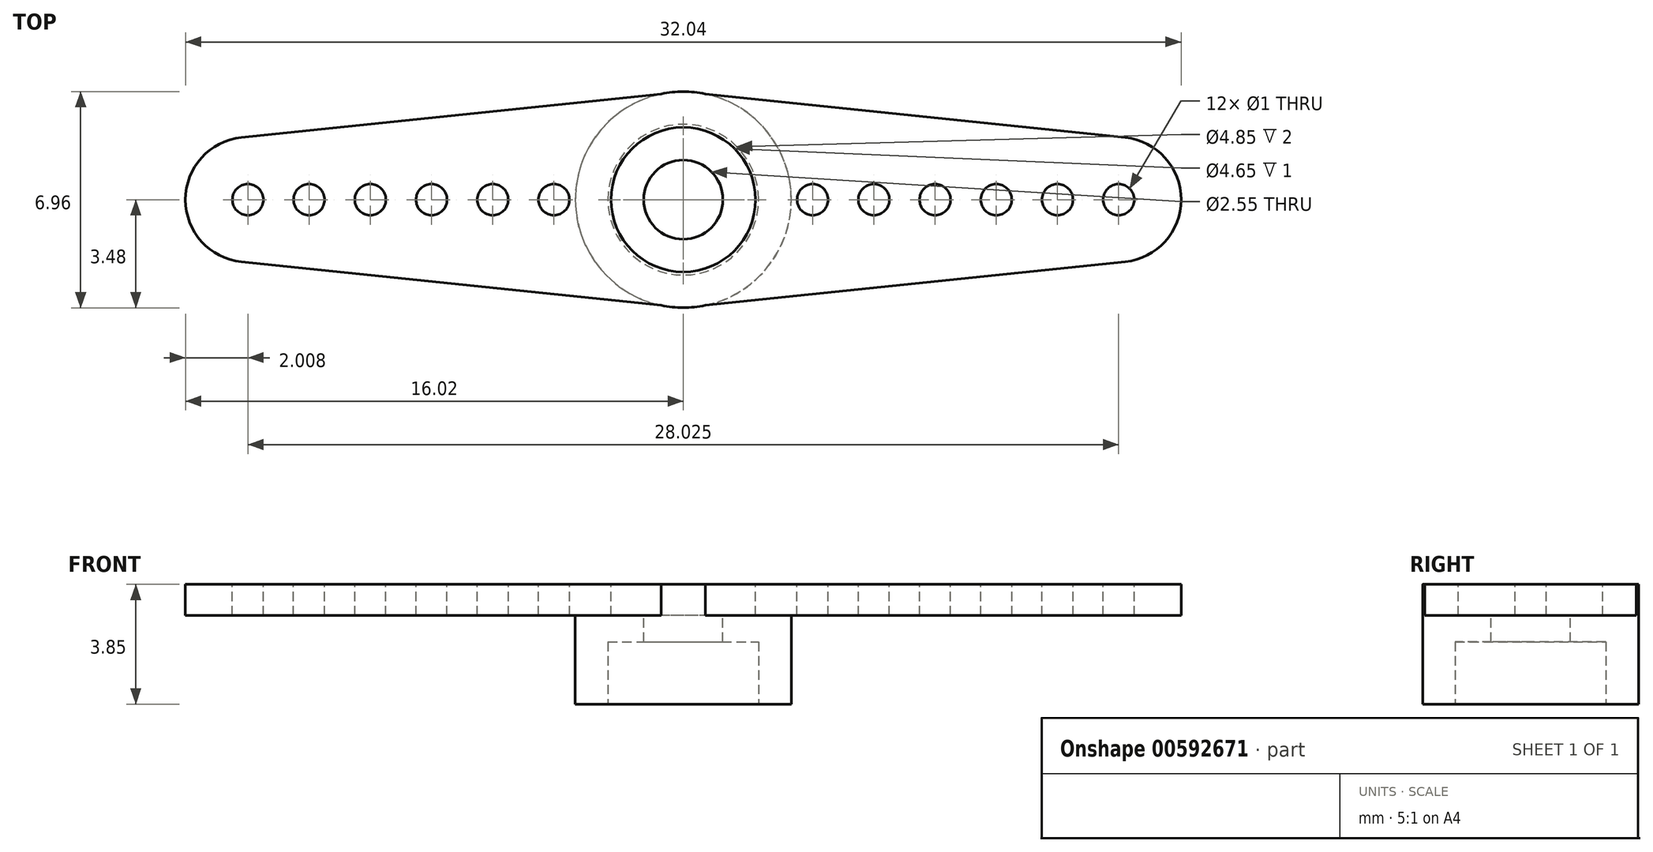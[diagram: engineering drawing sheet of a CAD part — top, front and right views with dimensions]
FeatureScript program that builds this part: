
annotation { "Feature Type Name" : "Feature", "Feature Type Description" : "" }
export const myFeature = defineFeature(function(context is Context, id is Id, definition is map)
    precondition{}
    {
        {
            var Q0;
            Q0=qCreatedBy(makeId("Top.planeOp"),FACE);
            var sketch = newSketch(context, id + "F0", { "sketchPlane" : qUnion([Q0])});
            skCircle(sketch, "E0", {"center": v(0, 0) * mm, "radius": 3.48 * mm});
            skSolve(sketch);
        }
        {
            var Q0;
            Q0=makeQuery(id+"F0.imprint","IMPRINT",FACE,{"disambiguationData":[TD([[makeQuery(id+"F0.imprint","IMPRINT",EDGE,{"derivedFrom":sQuery(id+"F0.wireOp",EDGE,"E0")}),1.0]])]});
            extrude(context, id + "F1", {"entities" : qUnion([Q0]), "depth" : 3.85 * mm, "offsetDistance" : 25 * mm});
        }
        {
            var Q0;
            Q0=makeQuery(id+"F1.opExtrude","CAP_FACE",FACE,{"disambiguationData":[OSD([sQuery(id+"F0.wireOp",EDGE,"E0")])],"isStart":true});
            var sketch = newSketch(context, id + "F2", { "sketchPlane" : qUnion([Q0])});
            skCircle(sketch, "E1", {"center": v(0, 0) * mm, "radius": 2.43 * mm});
            skSolve(sketch);
        }
        {
            var Q0;
            Q0=qSketchRegion(id+"F2",true);
            extrude(context, id + "F3", {"entities" : qUnion([Q0]), "operationType" : NewBodyOperationType.REMOVE, "oppositeDirection" : true, "depth" : 2 * mm, "offsetDistance" : 25 * mm});
        }
        {
            var Q0;
            Q0=makeQuery(id+"F1.opExtrude","CAP_FACE",FACE,{"disambiguationData":[OSD([sQuery(id+"F0.wireOp",EDGE,"E0")])],"isStart":false});
            var sketch = newSketch(context, id + "F4", { "sketchPlane" : qUnion([Q0])});
            skArc(sketch, "E2.0", {"start": v(0, 3.48) * mm, "mid": v(-3.48, 0) * mm, "end": v(0, -3.48) * mm});
            skLineSegment(sketch, "E3", {"start": v(0, 3.47) * mm, "end": v(14.22, 2) * mm});
            skLineSegment(sketch, "E4", {"start": v(0, -3.48) * mm, "end": v(14.22, -2) * mm});
            skLineSegment(sketch, "E5", {"start": v(0, 0) * mm, "end": v(14.22, 0) * mm, "construction": true});
            skLineSegment(sketch, "E6", {"start": v(14.22, 2) * mm, "end": v(14.22, 0) * mm, "construction": true});
            skLineSegment(sketch, "E7", {"start": v(14.22, 0) * mm, "end": v(14.22, -2) * mm, "construction": true});
            skArc(sketch, "E8", {"start": v(14.22, 2) * mm, "mid": v(16.02, 0) * mm, "end": v(14.22, -2) * mm});
            skSolve(sketch);
        }
        {
            var Q0;
            Q0=qSketchRegion(id+"F4",true);
            extrude(context, id + "F5", {"entities" : qUnion([Q0]), "operationType" : NewBodyOperationType.ADD, "oppositeDirection" : true, "depth" : 1 * mm, "offsetDistance" : 25 * mm});
        }
        {
            var Q0;
            Q0=makeQuery(id+"F5.boolean.opBoolean","MERGE",FACE,{"derivedFrom":[makeQuery(id+"F1.opExtrude","CAP_FACE",FACE,{"disambiguationData":[OSD([sQuery(id+"F0.wireOp",EDGE,"E0")])],"isStart":false}),makeQuery(id+"F5.opExtrude","CAP_FACE",FACE,{"disambiguationData":[OSD([sQuery(id+"F4.wireOp",EDGE,"E2.0"),sQuery(id+"F4.wireOp",EDGE,"E3"),sQuery(id+"F4.wireOp",EDGE,"E4"),sQuery(id+"F4.wireOp",EDGE,"E8")])],"isStart":true})]});
            var sketch = newSketch(context, id + "F6", { "sketchPlane" : qUnion([Q0])});
            skCircle(sketch, "E9", {"center": v(0, 0) * mm, "radius": 2.33 * mm});
            skSolve(sketch);
        }
        {
            var Q0;
            Q0=qSketchRegion(id+"F6",true);
            extrude(context, id + "F7", {"entities" : qUnion([Q0]), "operationType" : NewBodyOperationType.REMOVE, "oppositeDirection" : true, "depth" : 1 * mm, "offsetDistance" : 25 * mm});
        }
        {
            var Q0;
            Q0=makeQuery(id+"F7.boolean.opBoolean","COPY",FACE,{"derivedFrom":makeQuery(id+"F7.opExtrude","CAP_FACE",FACE,{"disambiguationData":[OSD([sQuery(id+"F6.wireOp",EDGE,"E9")])],"isStart":false})});
            var sketch = newSketch(context, id + "F8", { "sketchPlane" : qUnion([Q0])});
            skCircle(sketch, "E10", {"center": v(0, 0) * mm, "radius": 1.27 * mm});
            skSolve(sketch);
        }
        {
            var Q0;
            Q0=qSketchRegion(id+"F8",true);
            extrude(context, id + "F9", {"entities" : qUnion([Q0]), "operationType" : NewBodyOperationType.REMOVE, "endBound" : BoundingType.THROUGH_ALL, "oppositeDirection" : true, "depth" : 25 * mm, "offsetDistance" : 25 * mm});
        }
        {
            var Q0;
            Q0=makeQuery(id+"F5.boolean.opBoolean","MERGE",FACE,{"derivedFrom":[makeQuery(id+"F1.opExtrude","CAP_FACE",FACE,{"disambiguationData":[OSD([sQuery(id+"F0.wireOp",EDGE,"E0")])],"isStart":false}),makeQuery(id+"F5.opExtrude","CAP_FACE",FACE,{"disambiguationData":[OSD([sQuery(id+"F4.wireOp",EDGE,"E2.0"),sQuery(id+"F4.wireOp",EDGE,"E3"),sQuery(id+"F4.wireOp",EDGE,"E4"),sQuery(id+"F4.wireOp",EDGE,"E8")])],"isStart":true})]});
            var sketch = newSketch(context, id + "F10", { "sketchPlane" : qUnion([Q0])});
            skCircle(sketch, "E11", {"center": v(14.01, 0) * mm, "radius": 0.5 * mm});
            skCircle(sketch, "E12.1.0.0", {"center": v(12.04, 0) * mm, "radius": 0.5 * mm});
            skCircle(sketch, "E12.2.0.0", {"center": v(10.07, 0) * mm, "radius": 0.5 * mm});
            skCircle(sketch, "E12.3.0.0", {"center": v(8.1, 0) * mm, "radius": 0.5 * mm});
            skCircle(sketch, "E12.4.0.0", {"center": v(6.13, 0) * mm, "radius": 0.5 * mm});
            skCircle(sketch, "E12.5.0.0", {"center": v(4.16, 0) * mm, "radius": 0.5 * mm});
            skLineSegment(sketch, "E12.direction1", {"start": v(14.01, 0) * mm, "end": v(12.04, 0) * mm, "construction": true});
            skSolve(sketch);
        }
        {
            var Q0;
            Q0=qSketchRegion(id+"F10",true);
            extrude(context, id + "F11", {"entities" : qUnion([Q0]), "operationType" : NewBodyOperationType.REMOVE, "endBound" : BoundingType.THROUGH_ALL, "oppositeDirection" : true, "depth" : 25 * mm, "offsetDistance" : 25 * mm});
        }
        {
            var Q0;
            Q0=makeQuery(id+"F1.opExtrude","SWEPT_BODY",BODY,{"disambiguationData":[OSD([sQuery(id+"F0.wireOp",EDGE,"E0")])]});
            var Q1;
            Q1=qCreatedBy(makeId("Right.planeOp"),FACE);
            mirror(context, id + "F12", {"operationType" : NewBodyOperationType.ADD, "entities" : qUnion([Q0]), "mirrorPlane" : qUnion([Q1])});
        }
    });
